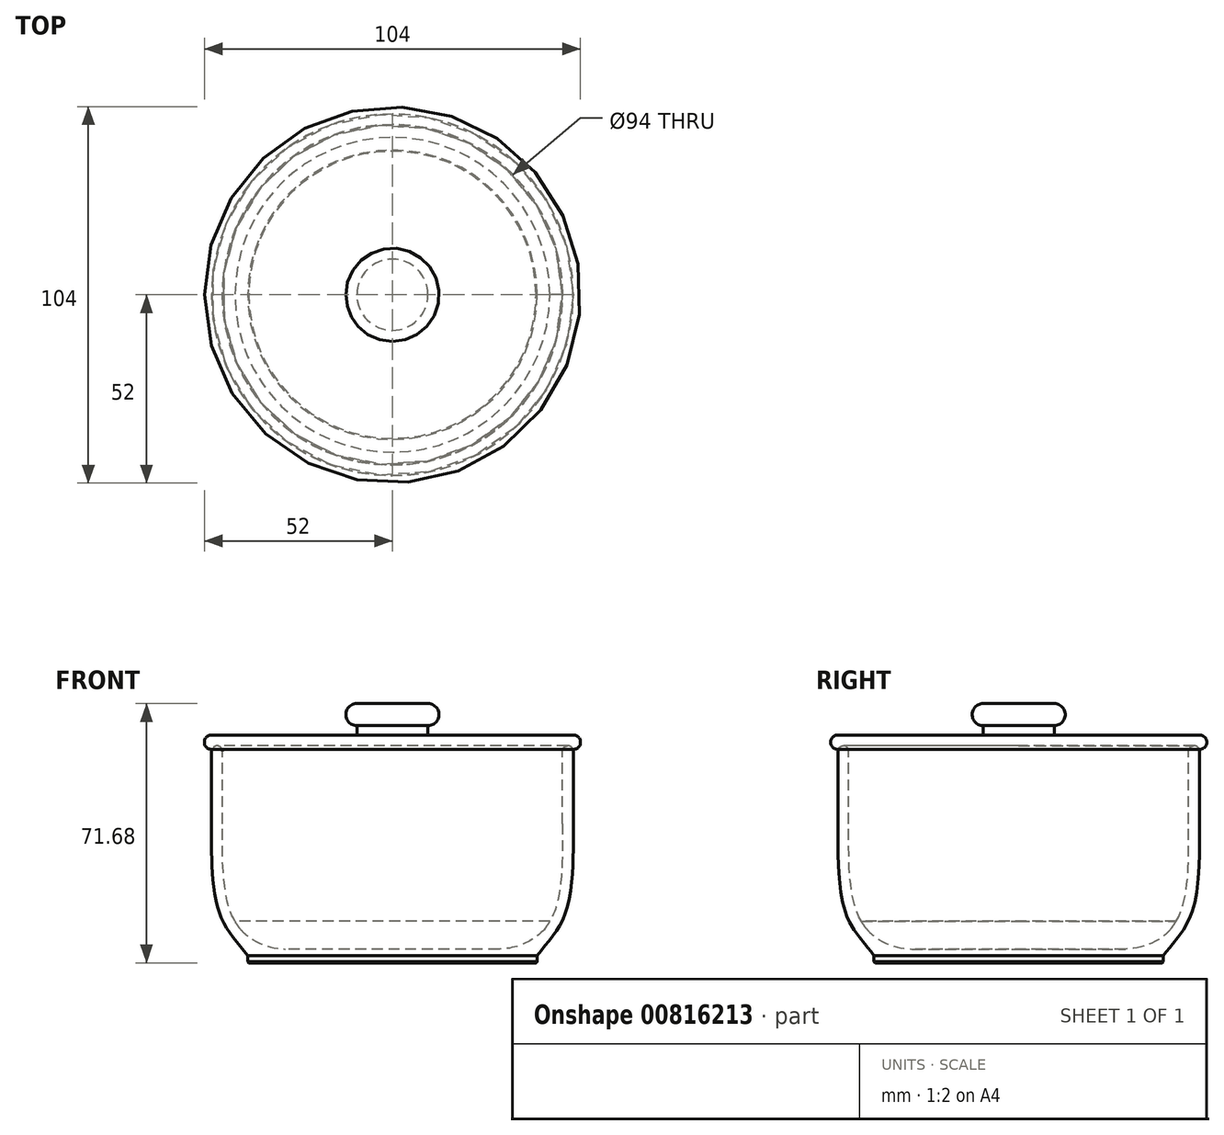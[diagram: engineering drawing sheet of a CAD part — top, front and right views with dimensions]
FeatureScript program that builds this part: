
annotation { "Feature Type Name" : "Feature", "Feature Type Description" : "" }
export const myFeature = defineFeature(function(context is Context, id is Id, definition is map)
    precondition{}
    {
        {
            var Q0;
            Q0=qCreatedBy(makeId("Front.planeOp"),FACE);
            var sketch = newSketch(context, id + "F0", { "sketchPlane" : qUnion([Q0])});
            skLineSegment(sketch, "E0", {"start": v(0, 0) * mm, "end": v(-40, 0) * mm});
            skLineSegment(sketch, "E1", {"start": v(-40, 0) * mm, "end": v(-40, 2) * mm});
            skLineSegment(sketch, "E2", {"start": v(-56.25, 60) * mm, "end": v(70.26, 60) * mm, "construction": true});
            skLineSegment(sketch, "E3", {"start": v(-50, 60) * mm, "end": v(-50, 40) * mm});
            skLineSegment(sketch, "E4", {"start": v(-57.59, 40) * mm, "end": v(68.7, 40) * mm, "construction": true});
            skFitSpline(sketch, "E5", {"points": [v(-50, 40) * mm, v(-50, 35.5) * mm, v(-48, 14.22) * mm, v(-40, 2) * mm], "startDerivative": vector(-0.06, -16.63) * mm, "endDerivative": vector(25.19, -33.33) * mm});
            skFitSpline(sketch, "E6.0", {"points": [v(-47, 39.99) * mm, v(-47, 39.65) * mm, v(-47, 39.13) * mm, v(-47, 38.33) * mm, v(-47, 37.64) * mm, v(-47, 36.99) * mm, v(-47, 36.4) * mm, v(-47, 36) * mm, v(-47, 35.67) * mm, v(-47, 35.33) * mm, v(-47, 34.69) * mm, v(-47, 33.3) * mm, v(-47, 31.01) * mm, v(-46.93, 27.94) * mm, v(-46.76, 24.7) * mm, v(-46.5, 21.98) * mm, v(-46.22, 19.9) * mm, v(-45.97, 18.38) * mm, v(-45.72, 17.2) * mm, v(-45.52, 16.41) * mm, v(-45.4, 15.98) * mm, v(-45.31, 15.67) * mm, v(-45.22, 15.36) * mm, v(-45.12, 15.06) * mm, v(-45.02, 14.77) * mm, v(-44.88, 14.39) * mm, v(-44.7, 13.93) * mm, v(-44.4, 13.22) * mm, v(-44, 12.38) * mm, v(-43.45, 11.42) * mm, v(-42.86, 10.5) * mm, v(-42.23, 9.6) * mm, v(-41.55, 8.7) * mm, v(-40.58, 7.5) * mm, v(-39.28, 5.93) * mm, v(-38.17, 4.55) * mm, v(-37.6, 3.8) * mm]});
            skLineSegment(sketch, "E6.1", {"start": v(-47, 60) * mm, "end": v(-47, 38.48) * mm});
            skLineSegment(sketch, "E7", {"start": v(-37.62, 3.82) * mm, "end": v(0, 3.82) * mm});
            skLineSegment(sketch, "E8", {"start": v(0, 3.82) * mm, "end": v(0, 0) * mm});
            skFitSpline(sketch, "E9", {"points": [v(-44.11, 12.64) * mm, v(-39.78, 7.23) * mm, v(-29.54, 3.82) * mm], "startDerivative": vector(7.83, -15.49) * mm, "endDerivative": vector(21.77, 0) * mm});
            skLineSegment(sketch, "E10", {"start": v(-50, 60) * mm, "end": v(-47, 60) * mm});
            skSolve(sketch);
        }
        {
            var Q0;
            Q0=makeQuery(id+"F0.imprint","IMPRINT",FACE,{"disambiguationData":[TD([[makeQuery(id+"F0.imprint","IMPRINT",EDGE,{"derivedFrom":sQuery(id+"F0.wireOp",EDGE,"E0")}),-1.0]])]});
            var Q1;
            {var subQ0=sQuery(id+"F0.wireOp",EDGE,"E7");var subQ1=sQuery(id+"F0.wireOp",EDGE,"E6.0");var subQ2=makeQuery(id+"F0.imprint","INTERSECT",VERTEX,{"derivedFrom":[subQ1,subQ0]});Q1=makeQuery(id+"F0.imprint","IMPRINT",FACE,{"disambiguationData":[TD([[makeQuery(id+"F0.imprint","IMPRINT",EDGE,{"disambiguationData":[TD([[subQ2,1.0]])],"derivedFrom":subQ1}),1.0]])]});}
            var Q2;
            Q2=sQuery(id+"F0.wireOp",EDGE,"E8");
            revolve(context, id + "F1", {"surfaceOperationType" : NewSurfaceOperationType.NEW, "entities" : qUnion([Q0, Q1]), "axis" : qUnion([Q2]), "revolveType" : RevolveType.FULL});
        }
        {
            var Q0;
            Q0=makeQuery(id+"F1.opRevolve","SWEPT_EDGE",EDGE,{"disambiguationData":[OSD([sQuery(id+"F0.wireOp",EDGE,"E0"),sQuery(id+"F0.wireOp",EDGE,"E1")])]});
            chamfer(context, id + "F2", {"entities" : qUnion([Q0]), "width" : 0.3 * mm, "tangentPropagation" : true});
        }
        {
            var Q0;
            Q0=makeQuery(id+"F1.opRevolve","SWEPT_FACE",FACE,{"disambiguationData":[OSD([sQuery(id+"F0.wireOp",EDGE,"E10")])]});
            fillet(context, id + "F3", {"entities" : qUnion([Q0]), "tangentPropagation" : true, "radius" : 1.5 * mm, "defaultsChanged" : true, "vertexSettings" : [], "allowEdgeOverflow" : false});
        }
        {
            var Q0;
            Q0=qCreatedBy(makeId("Front.planeOp"),FACE);
            var sketch = newSketch(context, id + "F4", { "sketchPlane" : qUnion([Q0])});
            skLineSegment(sketch, "E11.0", {"start": v(-50, 60) * mm, "end": v(-50, 40) * mm, "construction": true});
            skLineSegment(sketch, "E12.0", {"start": v(-47, 60) * mm, "end": v(-47, 38.48) * mm, "construction": true});
            skLineSegment(sketch, "E12.1", {"start": v(-50, 60) * mm, "end": v(-47, 60) * mm, "construction": true});
            skLineSegment(sketch, "E13", {"start": v(0, 59) * mm, "end": v(-52, 59) * mm});
            skLineSegment(sketch, "E14", {"start": v(-52, 59) * mm, "end": v(-52, 63) * mm});
            skLineSegment(sketch, "E15", {"start": v(0, 59) * mm, "end": v(0, 63) * mm});
            skLineSegment(sketch, "E16", {"start": v(-52, 63) * mm, "end": v(0, 63) * mm});
            skLineSegment(sketch, "E17.bottom", {"start": v(0, 63) * mm, "end": v(-9.83, 63) * mm});
            skLineSegment(sketch, "E17.top", {"start": v(0, 65.58) * mm, "end": v(-9.83, 65.58) * mm});
            skLineSegment(sketch, "E17.left", {"start": v(0, 63) * mm, "end": v(0, 65.58) * mm});
            skLineSegment(sketch, "E17.right", {"start": v(-9.83, 63) * mm, "end": v(-9.83, 65.58) * mm});
            skArc(sketch, "E18", {"start": v(-9.83, 71.68) * mm, "mid": v(-12.88, 68.63) * mm, "end": v(-9.83, 65.58) * mm});
            skLineSegment(sketch, "E19", {"start": v(-9.83, 71.68) * mm, "end": v(0, 71.68) * mm});
            skLineSegment(sketch, "E20", {"start": v(0, 71.68) * mm, "end": v(0, 65.58) * mm});
            skSolve(sketch);
        }
        {
            var Q0;
            Q0=makeQuery(id+"F4.imprint","IMPRINT",FACE,{"disambiguationData":[TD([[makeQuery(id+"F4.imprint","IMPRINT",EDGE,{"derivedFrom":sQuery(id+"F4.wireOp",EDGE,"E13")}),-1.0]])]});
            var Q1;
            Q1=makeQuery(id+"F4.imprint","IMPRINT",FACE,{"disambiguationData":[TD([[makeQuery(id+"F4.imprint","IMPRINT",EDGE,{"derivedFrom":sQuery(id+"F4.wireOp",EDGE,"E17.top")}),1.0]])]});
            var Q2;
            Q2=makeQuery(id+"F4.imprint","IMPRINT",FACE,{"disambiguationData":[TD([[makeQuery(id+"F4.imprint","IMPRINT",EDGE,{"derivedFrom":sQuery(id+"F4.wireOp",EDGE,"E17.top")}),-1.0]])]});
            var Q3;
            Q3=sQuery(id+"F4.wireOp",EDGE,"E15");
            revolve(context, id + "F5", {"surfaceOperationType" : NewSurfaceOperationType.NEW, "entities" : qUnion([Q0, Q1, Q2]), "axis" : qUnion([Q3]), "revolveType" : RevolveType.FULL});
        }
        {
            var Q0;
            Q0=makeQuery(id+"F5.opRevolve","SWEPT_FACE",FACE,{"disambiguationData":[OSD([sQuery(id+"F4.wireOp",EDGE,"E14")])]});
            fillet(context, id + "F6", {"entities" : qUnion([Q0]), "tangentPropagation" : true, "radius" : 2 * mm, "defaultsChanged" : true, "vertexSettings" : [], "allowEdgeOverflow" : false});
        }
        {
            var Q0;
            Q0=makeQuery(id+"F1.opRevolve","SWEPT_BODY",BODY,{"disambiguationData":[OSD([sQuery(id+"F0.wireOp",EDGE,"E0"),sQuery(id+"F0.wireOp",EDGE,"E1"),sQuery(id+"F0.wireOp",EDGE,"E3"),sQuery(id+"F0.wireOp",EDGE,"E5"),sQuery(id+"F0.wireOp",EDGE,"E6.0"),sQuery(id+"F0.wireOp",EDGE,"E6.1"),sQuery(id+"F0.wireOp",EDGE,"E7"),sQuery(id+"F0.wireOp",EDGE,"E8"),sQuery(id+"F0.wireOp",EDGE,"E9"),sQuery(id+"F0.wireOp",EDGE,"E10")])]});
            var Q1;
            Q1=makeQuery(id+"F5.opRevolve","SWEPT_BODY",BODY,{"disambiguationData":[OSD([sQuery(id+"F4.wireOp",EDGE,"E13"),sQuery(id+"F4.wireOp",EDGE,"E14"),sQuery(id+"F4.wireOp",EDGE,"E15"),sQuery(id+"F4.wireOp",EDGE,"924a54fd-4a53-4aa7-adad-314d63a097c8"),sQuery(id+"F4.wireOp",EDGE,"oOzf3ll2-zGG5-ojMz-reRt-95TYrPdoWAih"),sQuery(id+"F4.wireOp",EDGE,"RTjq6qX2-Shij-Zzct-dvOR-oadLS1goRqIS"),sQuery(id+"F4.wireOp",EDGE,"wnrF77RY-1uG4-mJbB-tT7A-edEf3FvErlft"),sQuery(id+"F4.wireOp",EDGE,"Utnal892-O40t-Mybl-Qgfy-DewwdLPbBhxS"),sQuery(id+"F4.wireOp",EDGE,"TvlzVIg8-BtZW-ihA9-6wut-CNLp48QDwk6Q")])]});
            booleanBodies(context, id + "F7", {"operationType" : BooleanOperationType.SUBTRACTION, "tools" : qUnion([Q0]), "targets" : qUnion([Q1]), "offsetAll" : true, "keepTools" : true});
        }
    });
